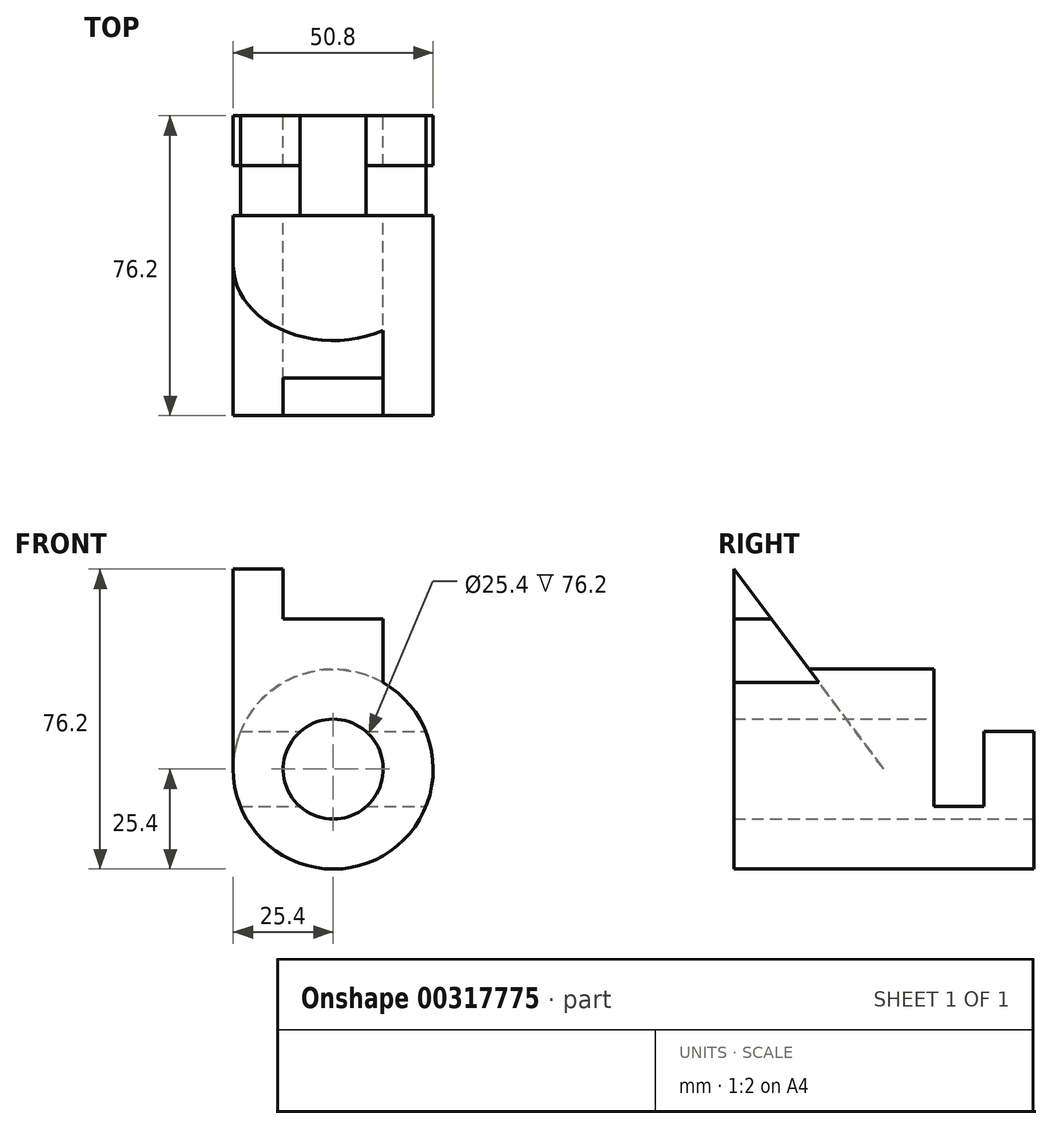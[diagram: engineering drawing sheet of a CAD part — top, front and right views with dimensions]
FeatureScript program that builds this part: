
annotation { "Feature Type Name" : "Feature", "Feature Type Description" : "" }
export const myFeature = defineFeature(function(context is Context, id is Id, definition is map)
    precondition{}
    {
        {
            var Q0;
            Q0=qCreatedBy(makeId("Front.planeOp"),FACE);
            var sketch = newSketch(context, id + "F0", { "sketchPlane" : qUnion([Q0])});
            skCircle(sketch, "E0", {"center": v(0, 0) * mm, "radius": 25.4 * mm});
            skCircle(sketch, "E1", {"center": v(0, 0) * mm, "radius": 12.7 * mm});
            skSolve(sketch);
        }
        {
            var Q0;
            Q0 = qSketchRegion(id + "F0", true);
            extrude(context, id + "F1", {"entities" : qUnion([Q0]), "depth" : 76.2 * mm});
        }
        {
            var Q0;
            Q0=qCreatedBy(makeId("Right.planeOp"),FACE);
            var sketch = newSketch(context, id + "F2", { "sketchPlane" : qUnion([Q0])});
            skLineSegment(sketch, "E2", {"start": v(-25.4, 42.26) * mm, "end": v(-25.4, -9.53) * mm});
            skLineSegment(sketch, "E3", {"start": v(-25.4, -9.53) * mm, "end": v(-12.7, -9.53) * mm});
            skLineSegment(sketch, "E4", {"start": v(-12.7, -9.53) * mm, "end": v(-12.7, 9.53) * mm});
            skLineSegment(sketch, "E5", {"start": v(-12.7, 9.53) * mm, "end": v(0, 9.53) * mm});
            skLineSegment(sketch, "E6", {"start": v(0, 9.53) * mm, "end": v(0, 42.26) * mm});
            skLineSegment(sketch, "E7", {"start": v(0, 42.26) * mm, "end": v(-25.4, 42.26) * mm});
            skSolve(sketch);
        }
        {
            var Q0;
            Q0 = qSketchRegion(id + "F2", true);
            extrude(context, id + "F3", {"entities" : qUnion([Q0]), "operationType" : NewBodyOperationType.REMOVE, "endBound" : BoundingType.THROUGH_ALL, "oppositeDirection" : true, "depth" : 25.4 * mm, "hasSecondDirection" : true, "secondDirectionBound" : SecondDirectionBoundingType.THROUGH_ALL, "secondDirectionOppositeDirection" : false, "secondDirectionDepth" : 25.4 * mm});
        }
        {
            var Q0;
            Q0=qCreatedBy(makeId("Right.planeOp"),FACE);
            var sketch = newSketch(context, id + "F4", { "sketchPlane" : qUnion([Q0])});
            skLineSegment(sketch, "E8", {"start": v(-76.2, 0) * mm, "end": v(-76.2, 50.8) * mm});
            skLineSegment(sketch, "E9", {"start": v(-76.2, 50.8) * mm, "end": v(-38.1, 0) * mm});
            skLineSegment(sketch, "E10", {"start": v(-38.1, 0) * mm, "end": v(-76.2, 0) * mm});
            skSolve(sketch);
        }
        {
            var Q0;
            Q0 = qSketchRegion(id + "F4", true);
            extrude(context, id + "F5", {"entities" : qUnion([Q0]), "operationType" : NewBodyOperationType.ADD, "depth" : 12.7 * mm, "hasSecondDirection" : true, "secondDirectionOppositeDirection" : true, "secondDirectionDepth" : 25.4 * mm});
        }
        {
            var Q0;
            Q0=makeQuery(id+"F5.boolean.opBoolean","MERGE",FACE,{"derivedFrom":[makeQuery(id+"F1.opExtrude","CAP_FACE",FACE,{"disambiguationData":[OSD([sQuery(id+"F0.wireOp",EDGE,"E0"),sQuery(id+"F0.wireOp",EDGE,"E1")])],"isStart":false}),makeQuery(id+"F5.opExtrude","SWEPT_FACE",FACE,{"disambiguationData":[OSD([sQuery(id+"F4.wireOp",EDGE,"E8")])]})]});
            var sketch = newSketch(context, id + "F6", { "sketchPlane" : qUnion([Q0])});
            skCircle(sketch, "E11", {"center": v(0, 0) * mm, "radius": 12.7 * mm});
            skSolve(sketch);
        }
        {
            var Q0;
            Q0 = qSketchRegion(id + "F6", true);
            extrude(context, id + "F7", {"entities" : qUnion([Q0]), "operationType" : NewBodyOperationType.REMOVE, "endBound" : BoundingType.THROUGH_ALL, "oppositeDirection" : true, "depth" : 25.4 * mm});
        }
        {
            var Q0;
            Q0=makeQuery(id+"F5.boolean.opBoolean","MERGE",FACE,{"derivedFrom":[makeQuery(id+"F1.opExtrude","CAP_FACE",FACE,{"disambiguationData":[OSD([sQuery(id+"F0.wireOp",EDGE,"E0"),sQuery(id+"F0.wireOp",EDGE,"E1")])],"isStart":false}),makeQuery(id+"F5.opExtrude","SWEPT_FACE",FACE,{"disambiguationData":[OSD([sQuery(id+"F4.wireOp",EDGE,"E8")])]})]});
            var sketch = newSketch(context, id + "F8", { "sketchPlane" : qUnion([Q0])});
            skLineSegment(sketch, "E12.bottom", {"start": v(12.7, 50.8) * mm, "end": v(-12.7, 50.8) * mm});
            skLineSegment(sketch, "E12.top", {"start": v(12.7, 38.1) * mm, "end": v(-12.7, 38.1) * mm});
            skLineSegment(sketch, "E12.left", {"start": v(12.7, 50.8) * mm, "end": v(12.7, 38.1) * mm});
            skLineSegment(sketch, "E12.right", {"start": v(-12.7, 50.8) * mm, "end": v(-12.7, 38.1) * mm});
            skSolve(sketch);
        }
        {
            var Q0;
            Q0 = qSketchRegion(id + "F8", true);
            extrude(context, id + "F9", {"entities" : qUnion([Q0]), "operationType" : NewBodyOperationType.REMOVE, "oppositeDirection" : true, "depth" : 25.4 * mm});
        }
    });
